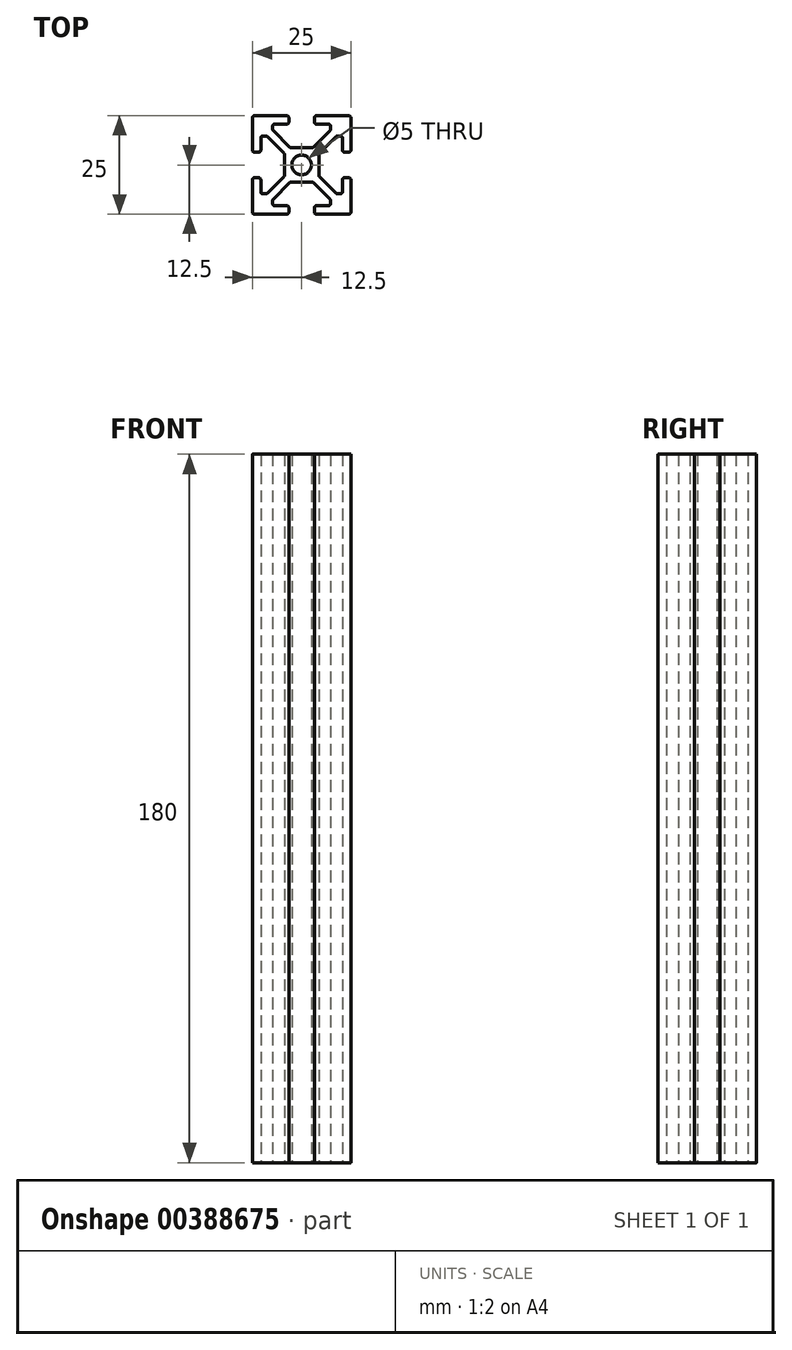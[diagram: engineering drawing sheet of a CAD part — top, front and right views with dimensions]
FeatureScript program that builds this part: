
annotation { "Feature Type Name" : "Feature", "Feature Type Description" : "" }
export const myFeature = defineFeature(function(context is Context, id is Id, definition is map)
    precondition{}
    {
        {
            var Q0;
            Q0=qCreatedBy(makeId("Top.planeOp"),FACE);
            var sketch = newSketch(context, id + "F0", { "sketchPlane" : qUnion([Q0])});
            skLineSegment(sketch, "E0.bottom", {"start": v(-12, 12.5) * mm, "end": v(-3.75, 12.5) * mm});
            skLineSegment(sketch, "E0.right", {"start": v(0, 12.5) * mm, "end": v(0, 4.38) * mm, "construction": true});
            skLineSegment(sketch, "E1", {"start": v(-3.25, 12) * mm, "end": v(-3.25, 10.87) * mm});
            skLineSegment(sketch, "E2", {"start": v(-3.75, 10.37) * mm, "end": v(-6.85, 10.37) * mm});
            skLineSegment(sketch, "E3", {"start": v(-7.35, 9.87) * mm, "end": v(-7.35, 9.06) * mm});
            skLineSegment(sketch, "E4", {"start": v(-7.2, 8.7) * mm, "end": v(-3.02, 4.53) * mm});
            skLineSegment(sketch, "E5", {"start": v(-2.67, 4.38) * mm, "end": v(0, 4.38) * mm});
            skLineSegment(sketch, "E6", {"start": v(-12.5, 12.5) * mm, "end": v(0, 0) * mm, "construction": true});
            skLineSegment(sketch, "E7", {"start": v(0, 4.38) * mm, "end": v(0, 2.5) * mm, "construction": true});
            skLineSegment(sketch, "E8", {"start": v(-3.25, 12.5) * mm, "end": v(0, 12.5) * mm, "construction": true});
            skLineSegment(sketch, "E9.MirrorCS", {"start": v(-10.37, 3.75) * mm, "end": v(-10.37, 6.84) * mm});
            skLineSegment(sketch, "E10.MirrorCS", {"start": v(-9.87, 7.34) * mm, "end": v(-9.06, 7.34) * mm});
            skLineSegment(sketch, "E11.MirrorCS", {"start": v(-8.7, 7.2) * mm, "end": v(-4.53, 3.02) * mm});
            skLineSegment(sketch, "E12.MirrorCS", {"start": v(-4.38, 2.67) * mm, "end": v(-4.38, 0) * mm});
            skLineSegment(sketch, "E13.MirrorCS", {"start": v(-12, 3.25) * mm, "end": v(-10.87, 3.25) * mm});
            skLineSegment(sketch, "E14.MirrorCS", {"start": v(-12.5, 12) * mm, "end": v(-12.5, 3.75) * mm});
            skLineSegment(sketch, "E15.MirrorCS", {"start": v(-4.38, 0) * mm, "end": v(-2.5, 0) * mm, "construction": true});
            skArc(sketch, "E16", {"start": v(0, 2.5) * mm, "mid": v(-0.96, 2.3) * mm, "end": v(-1.77, 1.77) * mm});
            skArc(sketch, "E17.MirrorCS", {"start": v(-2.5, 0) * mm, "mid": v(-2.3, 0.96) * mm, "end": v(-1.77, 1.77) * mm});
            skPoint(sketch, "E18.visualSharp", {"position": v(-7.35, 10.37) * mm});
            skArc(sketch, "E18.filletArc", {"start": v(-6.85, 10.37) * mm, "mid": v(-7.2, 10.22) * mm, "end": v(-7.35, 9.87) * mm});
            skPoint(sketch, "E19.visualSharp", {"position": v(-7.35, 8.85) * mm});
            skArc(sketch, "E19.filletArc", {"start": v(-7.35, 9.06) * mm, "mid": v(-7.3, 8.87) * mm, "end": v(-7.2, 8.7) * mm});
            skPoint(sketch, "E20.visualSharp", {"position": v(-2.87, 4.38) * mm});
            skArc(sketch, "E20.filletArc", {"start": v(-3.02, 4.53) * mm, "mid": v(-2.86, 4.42) * mm, "end": v(-2.67, 4.38) * mm});
            skPoint(sketch, "E21.visualSharp", {"position": v(-3.25, 10.37) * mm});
            skArc(sketch, "E21.filletArc", {"start": v(-3.75, 10.37) * mm, "mid": v(-3.4, 10.52) * mm, "end": v(-3.25, 10.87) * mm});
            skPoint(sketch, "E22.visualSharp", {"position": v(-3.25, 12.5) * mm});
            skArc(sketch, "E22.filletArc", {"start": v(-3.25, 12) * mm, "mid": v(-3.4, 12.35) * mm, "end": v(-3.75, 12.5) * mm});
            skPoint(sketch, "E23.visualSharp", {"position": v(-12.5, 12.5) * mm});
            skArc(sketch, "E23.filletArc", {"start": v(-12, 12.5) * mm, "mid": v(-12.35, 12.35) * mm, "end": v(-12.5, 12) * mm});
            skPoint(sketch, "E24.visualSharp", {"position": v(-10.37, 7.34) * mm});
            skArc(sketch, "E24.filletArc", {"start": v(-9.87, 7.34) * mm, "mid": v(-10.22, 7.2) * mm, "end": v(-10.37, 6.84) * mm});
            skPoint(sketch, "E25.visualSharp", {"position": v(-8.85, 7.34) * mm});
            skArc(sketch, "E25.filletArc", {"start": v(-8.7, 7.2) * mm, "mid": v(-8.87, 7.3) * mm, "end": v(-9.06, 7.34) * mm});
            skPoint(sketch, "E26.visualSharp", {"position": v(-10.37, 3.25) * mm});
            skArc(sketch, "E26.filletArc", {"start": v(-10.87, 3.25) * mm, "mid": v(-10.52, 3.4) * mm, "end": v(-10.37, 3.75) * mm});
            skPoint(sketch, "E27.visualSharp", {"position": v(-12.5, 3.25) * mm});
            skArc(sketch, "E27.filletArc", {"start": v(-12.5, 3.75) * mm, "mid": v(-12.35, 3.4) * mm, "end": v(-12, 3.25) * mm});
            skPoint(sketch, "E28.visualSharp", {"position": v(-4.38, 2.87) * mm});
            skArc(sketch, "E28.filletArc", {"start": v(-4.38, 2.67) * mm, "mid": v(-4.42, 2.86) * mm, "end": v(-4.53, 3.02) * mm});
            skArc(sketch, "E29.MirrorCS", {"start": v(-3.02, -4.53) * mm, "mid": v(-2.86, -4.42) * mm, "end": v(-2.67, -4.38) * mm});
            skArc(sketch, "E30.MirrorCS", {"start": v(-4.38, -2.67) * mm, "mid": v(-4.42, -2.86) * mm, "end": v(-4.53, -3.02) * mm});
            skArc(sketch, "E31.MirrorCS", {"start": v(-12.5, -3.75) * mm, "mid": v(-12.35, -3.4) * mm, "end": v(-12, -3.25) * mm});
            skArc(sketch, "E32.MirrorCS", {"start": v(-8.7, -7.2) * mm, "mid": v(-8.87, -7.3) * mm, "end": v(-9.06, -7.34) * mm});
            skArc(sketch, "E33.MirrorCS", {"start": v(-7.34, -9.06) * mm, "mid": v(-7.3, -8.87) * mm, "end": v(-7.2, -8.7) * mm});
            skLineSegment(sketch, "E34.MirrorCS", {"start": v(-7.34, -9.87) * mm, "end": v(-7.34, -9.06) * mm});
            skArc(sketch, "E35.MirrorCS", {"start": v(-3.75, -10.37) * mm, "mid": v(-3.4, -10.52) * mm, "end": v(-3.25, -10.87) * mm});
            skArc(sketch, "E36.MirrorCS", {"start": v(-9.87, -7.35) * mm, "mid": v(-10.22, -7.2) * mm, "end": v(-10.37, -6.85) * mm});
            skArc(sketch, "E37.MirrorCS", {"start": v(-12, -12.5) * mm, "mid": v(-12.35, -12.35) * mm, "end": v(-12.5, -12) * mm});
            skLineSegment(sketch, "E38.MirrorCS", {"start": v(-12, -3.25) * mm, "end": v(-10.87, -3.25) * mm});
            skArc(sketch, "E39.MirrorCS", {"start": v(-6.84, -10.37) * mm, "mid": v(-7.2, -10.22) * mm, "end": v(-7.34, -9.87) * mm});
            skArc(sketch, "E40.MirrorCS", {"start": v(-3.25, -12) * mm, "mid": v(-3.4, -12.35) * mm, "end": v(-3.75, -12.5) * mm});
            skArc(sketch, "E41.MirrorCS", {"start": v(-10.87, -3.25) * mm, "mid": v(-10.52, -3.4) * mm, "end": v(-10.37, -3.75) * mm});
            skLineSegment(sketch, "E42.MirrorCS", {"start": v(-9.87, -7.35) * mm, "end": v(-9.06, -7.35) * mm});
            skLineSegment(sketch, "E43.MirrorCS", {"start": v(0, -4.38) * mm, "end": v(0, -2.5) * mm, "construction": true});
            skLineSegment(sketch, "E44.MirrorCS", {"start": v(-3.25, -12) * mm, "end": v(-3.25, -10.87) * mm});
            skPoint(sketch, "E45.MirrorP", {"position": v(-12.5, -12.5) * mm});
            skArc(sketch, "E46.MirrorCS", {"start": v(-2.5, 0) * mm, "mid": v(-2.3, -0.96) * mm, "end": v(-1.77, -1.77) * mm});
            skPoint(sketch, "E47.MirrorP", {"position": v(-2.87, -4.38) * mm});
            skPoint(sketch, "E48.MirrorP", {"position": v(-4.38, -2.87) * mm});
            skPoint(sketch, "E49.MirrorP", {"position": v(-12.5, -3.25) * mm});
            skLineSegment(sketch, "E50.MirrorCS", {"start": v(-12.5, -12) * mm, "end": v(-12.5, -3.75) * mm});
            skLineSegment(sketch, "E51.MirrorCS", {"start": v(-12, -12.5) * mm, "end": v(-3.75, -12.5) * mm});
            skLineSegment(sketch, "E52.MirrorCS", {"start": v(0, -12.5) * mm, "end": v(0, -4.38) * mm, "construction": true});
            skPoint(sketch, "E53.MirrorP", {"position": v(-7.34, -8.85) * mm});
            skPoint(sketch, "E54.MirrorP", {"position": v(-3.25, -12.5) * mm});
            skPoint(sketch, "E55.MirrorP", {"position": v(-10.37, -7.35) * mm});
            skLineSegment(sketch, "E56.MirrorCS", {"start": v(-2.67, -4.38) * mm, "end": v(0, -4.38) * mm});
            skLineSegment(sketch, "E57.MirrorCS", {"start": v(-7.2, -8.7) * mm, "end": v(-3.02, -4.53) * mm});
            skPoint(sketch, "E58.MirrorP", {"position": v(-7.34, -10.37) * mm});
            skLineSegment(sketch, "E59.MirrorCS", {"start": v(-10.37, -3.75) * mm, "end": v(-10.37, -6.85) * mm});
            skArc(sketch, "E60.MirrorCS", {"start": v(0, -2.5) * mm, "mid": v(-0.96, -2.3) * mm, "end": v(-1.77, -1.77) * mm});
            skPoint(sketch, "E61.MirrorP", {"position": v(-8.85, -7.35) * mm});
            skLineSegment(sketch, "E62.MirrorCS", {"start": v(-8.7, -7.2) * mm, "end": v(-4.53, -3.02) * mm});
            skLineSegment(sketch, "E63.MirrorCS", {"start": v(-3.75, -10.37) * mm, "end": v(-6.84, -10.37) * mm});
            skPoint(sketch, "E64.MirrorP", {"position": v(-3.25, -10.37) * mm});
            skPoint(sketch, "E65.MirrorP", {"position": v(-10.37, -3.25) * mm});
            skLineSegment(sketch, "E66.MirrorCS", {"start": v(-12.5, -12.5) * mm, "end": v(0, 0) * mm, "construction": true});
            skLineSegment(sketch, "E67.MirrorCS", {"start": v(-3.25, -12.5) * mm, "end": v(0, -12.5) * mm, "construction": true});
            skLineSegment(sketch, "E68.MirrorCS", {"start": v(-4.38, -2.67) * mm, "end": v(-4.38, 0) * mm});
            skArc(sketch, "E69.MirrorCS", {"start": v(7.35, -9.06) * mm, "mid": v(7.3, -8.87) * mm, "end": v(7.2, -8.7) * mm});
            skArc(sketch, "E70.MirrorCS", {"start": v(8.7, -7.2) * mm, "mid": v(8.87, -7.3) * mm, "end": v(9.06, -7.34) * mm});
            skArc(sketch, "E71.MirrorCS", {"start": v(3.25, 12) * mm, "mid": v(3.4, 12.35) * mm, "end": v(3.75, 12.5) * mm});
            skLineSegment(sketch, "E72.MirrorCS", {"start": v(7.34, 9.87) * mm, "end": v(7.34, 9.06) * mm});
            skLineSegment(sketch, "E73.MirrorCS", {"start": v(3.25, 12) * mm, "end": v(3.25, 10.87) * mm});
            skArc(sketch, "E74.MirrorCS", {"start": v(4.38, -2.67) * mm, "mid": v(4.42, -2.86) * mm, "end": v(4.53, -3.02) * mm});
            skArc(sketch, "E75.MirrorCS", {"start": v(12, -12.5) * mm, "mid": v(12.35, -12.35) * mm, "end": v(12.5, -12) * mm});
            skArc(sketch, "E76.MirrorCS", {"start": v(3.02, 4.53) * mm, "mid": v(2.86, 4.42) * mm, "end": v(2.67, 4.38) * mm});
            skArc(sketch, "E77.MirrorCS", {"start": v(4.38, 2.67) * mm, "mid": v(4.42, 2.86) * mm, "end": v(4.53, 3.02) * mm});
            skArc(sketch, "E78.MirrorCS", {"start": v(12.5, 3.75) * mm, "mid": v(12.35, 3.4) * mm, "end": v(12, 3.25) * mm});
            skLineSegment(sketch, "E79.MirrorCS", {"start": v(7.35, -9.87) * mm, "end": v(7.35, -9.06) * mm});
            skArc(sketch, "E80.MirrorCS", {"start": v(3.02, -4.53) * mm, "mid": v(2.86, -4.42) * mm, "end": v(2.67, -4.38) * mm});
            skArc(sketch, "E81.MirrorCS", {"start": v(8.7, 7.2) * mm, "mid": v(8.87, 7.3) * mm, "end": v(9.06, 7.35) * mm});
            skLineSegment(sketch, "E82.MirrorCS", {"start": v(3.25, -12) * mm, "end": v(3.25, -10.87) * mm});
            skArc(sketch, "E83.MirrorCS", {"start": v(9.87, -7.34) * mm, "mid": v(10.22, -7.2) * mm, "end": v(10.37, -6.84) * mm});
            skArc(sketch, "E84.MirrorCS", {"start": v(7.34, 9.06) * mm, "mid": v(7.3, 8.87) * mm, "end": v(7.2, 8.7) * mm});
            skLineSegment(sketch, "E85.MirrorCS", {"start": v(9.87, -7.34) * mm, "end": v(9.06, -7.34) * mm});
            skArc(sketch, "E86.MirrorCS", {"start": v(3.75, -10.37) * mm, "mid": v(3.4, -10.52) * mm, "end": v(3.25, -10.87) * mm});
            skArc(sketch, "E87.MirrorCS", {"start": v(9.87, 7.35) * mm, "mid": v(10.22, 7.2) * mm, "end": v(10.37, 6.85) * mm});
            skArc(sketch, "E88.MirrorCS", {"start": v(3.25, -12) * mm, "mid": v(3.4, -12.35) * mm, "end": v(3.75, -12.5) * mm});
            skArc(sketch, "E89.MirrorCS", {"start": v(12, 12.5) * mm, "mid": v(12.35, 12.35) * mm, "end": v(12.5, 12) * mm});
            skArc(sketch, "E90.MirrorCS", {"start": v(6.85, -10.37) * mm, "mid": v(7.2, -10.22) * mm, "end": v(7.35, -9.87) * mm});
            skArc(sketch, "E91.MirrorCS", {"start": v(12.5, -3.75) * mm, "mid": v(12.35, -3.4) * mm, "end": v(12, -3.25) * mm});
            skLineSegment(sketch, "E92.MirrorCS", {"start": v(12, -3.25) * mm, "end": v(10.87, -3.25) * mm});
            skLineSegment(sketch, "E93.MirrorCS", {"start": v(9.87, 7.35) * mm, "end": v(9.06, 7.35) * mm});
            skLineSegment(sketch, "E94.MirrorCS", {"start": v(12, 3.25) * mm, "end": v(10.87, 3.25) * mm});
            skArc(sketch, "E95.MirrorCS", {"start": v(3.75, 10.37) * mm, "mid": v(3.4, 10.52) * mm, "end": v(3.25, 10.87) * mm});
            skArc(sketch, "E96.MirrorCS", {"start": v(2.5, 0) * mm, "mid": v(2.3, -0.96) * mm, "end": v(1.77, -1.77) * mm});
            skArc(sketch, "E97.MirrorCS", {"start": v(6.84, 10.37) * mm, "mid": v(7.2, 10.22) * mm, "end": v(7.34, 9.87) * mm});
            skArc(sketch, "E98.MirrorCS", {"start": v(10.87, -3.25) * mm, "mid": v(10.52, -3.4) * mm, "end": v(10.37, -3.75) * mm});
            skArc(sketch, "E99.MirrorCS", {"start": v(10.87, 3.25) * mm, "mid": v(10.52, 3.4) * mm, "end": v(10.37, 3.75) * mm});
            skPoint(sketch, "E100.MirrorP", {"position": v(7.34, 10.37) * mm});
            skPoint(sketch, "E101.MirrorP", {"position": v(10.37, 3.25) * mm});
            skLineSegment(sketch, "E102.MirrorCS", {"start": v(2.67, -4.38) * mm, "end": v(0, -4.38) * mm});
            skArc(sketch, "E103.MirrorCS", {"start": v(2.5, 0) * mm, "mid": v(2.3, 0.96) * mm, "end": v(1.77, 1.77) * mm});
            skLineSegment(sketch, "E104.MirrorCS", {"start": v(3.25, -12.5) * mm, "end": v(0, -12.5) * mm, "construction": true});
            skPoint(sketch, "E105.MirrorP", {"position": v(10.37, -7.34) * mm});
            skArc(sketch, "E106.MirrorCS", {"start": v(0, 2.5) * mm, "mid": v(0.96, 2.3) * mm, "end": v(1.77, 1.77) * mm});
            skPoint(sketch, "E107.MirrorP", {"position": v(3.25, -12.5) * mm});
            skLineSegment(sketch, "E108.MirrorCS", {"start": v(12.5, -12.5) * mm, "end": v(0, 0) * mm, "construction": true});
            skPoint(sketch, "E109.MirrorP", {"position": v(3.25, 12.5) * mm});
            skLineSegment(sketch, "E110.MirrorCS", {"start": v(12, -12.5) * mm, "end": v(3.75, -12.5) * mm});
            skLineSegment(sketch, "E111.MirrorCS", {"start": v(4.38, 0) * mm, "end": v(2.5, 0) * mm, "construction": true});
            skPoint(sketch, "E112.MirrorP", {"position": v(7.35, -8.85) * mm});
            skLineSegment(sketch, "E113.MirrorCS", {"start": v(3.75, -10.37) * mm, "end": v(6.85, -10.37) * mm});
            skPoint(sketch, "E114.MirrorP", {"position": v(8.85, 7.35) * mm});
            skPoint(sketch, "E115.MirrorP", {"position": v(10.37, -3.25) * mm});
            skLineSegment(sketch, "E116.MirrorCS", {"start": v(8.7, 7.2) * mm, "end": v(4.53, 3.02) * mm});
            skLineSegment(sketch, "E117.MirrorCS", {"start": v(10.37, 3.75) * mm, "end": v(10.37, 6.85) * mm});
            skLineSegment(sketch, "E118.MirrorCS", {"start": v(3.25, 12.5) * mm, "end": v(0, 12.5) * mm, "construction": true});
            skLineSegment(sketch, "E119.MirrorCS", {"start": v(0, 4.38) * mm, "end": v(0, 2.5) * mm});
            skLineSegment(sketch, "E120.MirrorCS", {"start": v(12.5, 12.5) * mm, "end": v(0, 0) * mm, "construction": true});
            skLineSegment(sketch, "E121.MirrorCS", {"start": v(2.67, 4.38) * mm, "end": v(0, 4.38) * mm});
            skLineSegment(sketch, "E122.MirrorCS", {"start": v(7.2, 8.7) * mm, "end": v(3.02, 4.53) * mm});
            skLineSegment(sketch, "E123.MirrorCS", {"start": v(3.75, 10.37) * mm, "end": v(6.84, 10.37) * mm});
            skLineSegment(sketch, "E124.MirrorCS", {"start": v(12, 12.5) * mm, "end": v(3.75, 12.5) * mm});
            skLineSegment(sketch, "E125.MirrorCS", {"start": v(12.5, 12) * mm, "end": v(12.5, 3.75) * mm});
            skLineSegment(sketch, "E126.MirrorCS", {"start": v(4.38, 2.67) * mm, "end": v(4.38, 0) * mm});
            skLineSegment(sketch, "E127.MirrorCS", {"start": v(12.5, -12) * mm, "end": v(12.5, -3.75) * mm});
            skLineSegment(sketch, "E128.MirrorCS", {"start": v(8.7, -7.2) * mm, "end": v(4.53, -3.02) * mm});
            skPoint(sketch, "E129.MirrorP", {"position": v(12.5, 12.5) * mm});
            skPoint(sketch, "E130.MirrorP", {"position": v(3.25, -10.37) * mm});
            skPoint(sketch, "E131.MirrorP", {"position": v(7.35, -10.37) * mm});
            skLineSegment(sketch, "E132.MirrorCS", {"start": v(7.2, -8.7) * mm, "end": v(3.02, -4.53) * mm});
            skPoint(sketch, "E133.MirrorP", {"position": v(12.5, 3.25) * mm});
            skPoint(sketch, "E134.MirrorP", {"position": v(10.37, 7.35) * mm});
            skArc(sketch, "E135.MirrorCS", {"start": v(0, -2.5) * mm, "mid": v(0.96, -2.3) * mm, "end": v(1.77, -1.77) * mm});
            skPoint(sketch, "E136.MirrorP", {"position": v(12.5, -12.5) * mm});
            skPoint(sketch, "E137.MirrorP", {"position": v(7.34, 8.85) * mm});
            skPoint(sketch, "E138.MirrorP", {"position": v(8.85, -7.34) * mm});
            skPoint(sketch, "E139.MirrorP", {"position": v(4.38, -2.87) * mm});
            skPoint(sketch, "E140.MirrorP", {"position": v(3.25, 10.37) * mm});
            skLineSegment(sketch, "E141.MirrorCS", {"start": v(4.38, -2.67) * mm, "end": v(4.38, 0) * mm});
            skPoint(sketch, "E142.MirrorP", {"position": v(12.5, -3.25) * mm});
            skPoint(sketch, "E143.MirrorP", {"position": v(2.87, -4.38) * mm});
            skPoint(sketch, "E144.MirrorP", {"position": v(4.38, 2.87) * mm});
            skLineSegment(sketch, "E145.MirrorCS", {"start": v(10.37, -3.75) * mm, "end": v(10.37, -6.84) * mm});
            skPoint(sketch, "E146.MirrorP", {"position": v(2.87, 4.38) * mm});
            skSolve(sketch);
        }
        {
            var Q0;
            Q0 = qSketchRegion(id + "F0", true);
            extrude(context, id + "F1", {"entities" : qUnion([Q0]), "depth" : 180 * mm});
        }
    });
